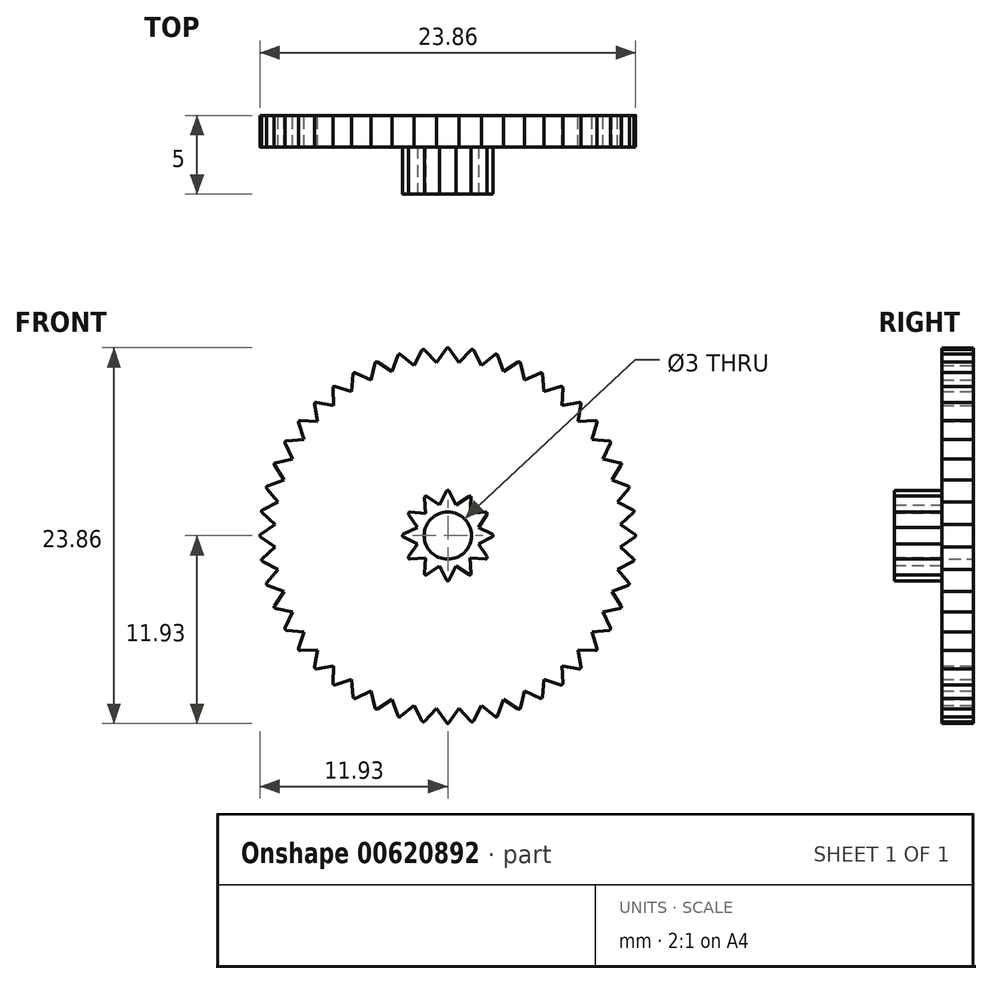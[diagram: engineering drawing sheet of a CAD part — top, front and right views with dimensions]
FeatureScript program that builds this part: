
annotation { "Feature Type Name" : "Feature", "Feature Type Description" : "" }
export const myFeature = defineFeature(function(context is Context, id is Id, definition is map)
    precondition{}
    {
        {
            var Q0;
            Q0=qCreatedBy(makeId("Front.planeOp"),FACE);
            var sketch = newSketch(context, id + "F0", { "sketchPlane" : qUnion([Q0])});
            skCircle(sketch, "E0", {"center": v(0, 0) * mm, "radius": 11 * mm});
            skLineSegment(sketch, "E1", {"start": v(0, 12) * mm, "end": v(0, 11) * mm, "construction": true});
            skCircle(sketch, "E2", {"center": v(0, 0) * mm, "radius": 1.5 * mm});
            skLineSegment(sketch, "E3", {"start": v(0, 12) * mm, "end": v(-0.72, 10.98) * mm});
            skLineSegment(sketch, "E4.MirrorCS", {"start": v(0, 12) * mm, "end": v(0.72, 10.98) * mm});
            skSolve(sketch);
        }
        {
            var Q0;
            Q0=makeQuery(id+"F0.imprint","IMPRINT",FACE,{"disambiguationData":[TD([[makeQuery(id+"F0.imprint","IMPRINT",EDGE,{"derivedFrom":sQuery(id+"F0.wireOp",EDGE,"E2")}),-1.0]])]});
            extrude(context, id + "F1", {"entities" : qUnion([Q0]), "depth" : 2 * mm, "offsetDistance" : 25 * mm});
        }
        {
            var Q0;
            {var subQ0=sQuery(id+"F0.wireOp",EDGE,"E3");Q0=makeQuery(id+"F0.imprint","IMPRINT",FACE,{"disambiguationData":[TD([[makeQuery(id+"F0.imprint","IMPRINT",EDGE,{"derivedFrom":subQ0}),1.0]])]});}
            extrude(context, id + "F2", {"entities" : qUnion([Q0]), "depth" : 2 * mm, "offsetDistance" : 25 * mm});
        }
        {
            var Q0;
            Q0=makeQuery(id+"F2.opExtrude","SWEPT_EDGE",EDGE,{"disambiguationData":[OSD([sQuery(id+"F0.wireOp",EDGE,"E3"),sQuery(id+"F0.wireOp",EDGE,"E4.MirrorCS")])]});
            fillet(context, id + "F3", {"entities" : qUnion([Q0]), "radius" : 0.1 * mm, "tangentPropagation" : true, "allowEdgeOverflow" : false});
        }
        {
            var Q0;
            Q0=makeQuery(id+"F2.opExtrude","SWEPT_BODY",BODY,{"disambiguationData":[OSD([sQuery(id+"F0.wireOp",EDGE,"E0"),sQuery(id+"F0.wireOp",EDGE,"E3"),sQuery(id+"F0.wireOp",EDGE,"E4.MirrorCS")])]});
            var Q1;
            Q1=makeQuery(id+"F1.opExtrude","CAP_EDGE",EDGE,{"disambiguationData":[OSD([sQuery(id+"F0.wireOp",EDGE,"E2")])],"isStart":false});
            circularPattern(context, id + "F4", {"operationType" : NewBodyOperationType.ADD, "entities" : qUnion([Q0]), "axis" : qUnion([Q1]), "angle" : 360 * degree, "instanceCount" : 48, "equalSpace" : true});
        }
        {
            var Q0;
            {var subQ0=sQuery(id+"F0.wireOp",EDGE,"E0");var subQ1=makeQuery(id+"F2.opExtrude","CAP_FACE",FACE,{"disambiguationData":[OSD([subQ0,sQuery(id+"F0.wireOp",EDGE,"E3"),sQuery(id+"F0.wireOp",EDGE,"E4.MirrorCS")])],"isStart":false});Q0=makeQuery(id+"F4.boolean.opBoolean","MERGE",FACE,{"derivedFrom":[makeQuery(id+"F1.opExtrude","CAP_FACE",FACE,{"disambiguationData":[OSD([subQ0,sQuery(id+"F0.wireOp",EDGE,"E2")])],"isStart":false}),subQ1,makeQuery(id+"F4.opPattern","COPY",FACE,{"derivedFrom":subQ1,"instanceName":"1"}),makeQuery(id+"F4.opPattern","COPY",FACE,{"derivedFrom":subQ1,"instanceName":"2"}),makeQuery(id+"F4.opPattern","COPY",FACE,{"derivedFrom":subQ1,"instanceName":"3"}),makeQuery(id+"F4.opPattern","COPY",FACE,{"derivedFrom":subQ1,"instanceName":"4"}),makeQuery(id+"F4.opPattern","COPY",FACE,{"derivedFrom":subQ1,"instanceName":"5"}),makeQuery(id+"F4.opPattern","COPY",FACE,{"derivedFrom":subQ1,"instanceName":"6"}),makeQuery(id+"F4.opPattern","COPY",FACE,{"derivedFrom":subQ1,"instanceName":"7"}),makeQuery(id+"F4.opPattern","COPY",FACE,{"derivedFrom":subQ1,"instanceName":"8"}),makeQuery(id+"F4.opPattern","COPY",FACE,{"derivedFrom":subQ1,"instanceName":"9"}),makeQuery(id+"F4.opPattern","COPY",FACE,{"derivedFrom":subQ1,"instanceName":"10"}),makeQuery(id+"F4.opPattern","COPY",FACE,{"derivedFrom":subQ1,"instanceName":"11"}),makeQuery(id+"F4.opPattern","COPY",FACE,{"derivedFrom":subQ1,"instanceName":"12"}),makeQuery(id+"F4.opPattern","COPY",FACE,{"derivedFrom":subQ1,"instanceName":"13"}),makeQuery(id+"F4.opPattern","COPY",FACE,{"derivedFrom":subQ1,"instanceName":"14"}),makeQuery(id+"F4.opPattern","COPY",FACE,{"derivedFrom":subQ1,"instanceName":"15"}),makeQuery(id+"F4.opPattern","COPY",FACE,{"derivedFrom":subQ1,"instanceName":"16"}),makeQuery(id+"F4.opPattern","COPY",FACE,{"derivedFrom":subQ1,"instanceName":"17"}),makeQuery(id+"F4.opPattern","COPY",FACE,{"derivedFrom":subQ1,"instanceName":"18"}),makeQuery(id+"F4.opPattern","COPY",FACE,{"derivedFrom":subQ1,"instanceName":"19"}),makeQuery(id+"F4.opPattern","COPY",FACE,{"derivedFrom":subQ1,"instanceName":"20"}),makeQuery(id+"F4.opPattern","COPY",FACE,{"derivedFrom":subQ1,"instanceName":"21"}),makeQuery(id+"F4.opPattern","COPY",FACE,{"derivedFrom":subQ1,"instanceName":"22"}),makeQuery(id+"F4.opPattern","COPY",FACE,{"derivedFrom":subQ1,"instanceName":"23"}),makeQuery(id+"F4.opPattern","COPY",FACE,{"derivedFrom":subQ1,"instanceName":"24"}),makeQuery(id+"F4.opPattern","COPY",FACE,{"derivedFrom":subQ1,"instanceName":"25"}),makeQuery(id+"F4.opPattern","COPY",FACE,{"derivedFrom":subQ1,"instanceName":"26"}),makeQuery(id+"F4.opPattern","COPY",FACE,{"derivedFrom":subQ1,"instanceName":"27"}),makeQuery(id+"F4.opPattern","COPY",FACE,{"derivedFrom":subQ1,"instanceName":"28"}),makeQuery(id+"F4.opPattern","COPY",FACE,{"derivedFrom":subQ1,"instanceName":"29"}),makeQuery(id+"F4.opPattern","COPY",FACE,{"derivedFrom":subQ1,"instanceName":"30"}),makeQuery(id+"F4.opPattern","COPY",FACE,{"derivedFrom":subQ1,"instanceName":"31"}),makeQuery(id+"F4.opPattern","COPY",FACE,{"derivedFrom":subQ1,"instanceName":"32"}),makeQuery(id+"F4.opPattern","COPY",FACE,{"derivedFrom":subQ1,"instanceName":"33"}),makeQuery(id+"F4.opPattern","COPY",FACE,{"derivedFrom":subQ1,"instanceName":"34"}),makeQuery(id+"F4.opPattern","COPY",FACE,{"derivedFrom":subQ1,"instanceName":"35"}),makeQuery(id+"F4.opPattern","COPY",FACE,{"derivedFrom":subQ1,"instanceName":"36"}),makeQuery(id+"F4.opPattern","COPY",FACE,{"derivedFrom":subQ1,"instanceName":"37"}),makeQuery(id+"F4.opPattern","COPY",FACE,{"derivedFrom":subQ1,"instanceName":"38"}),makeQuery(id+"F4.opPattern","COPY",FACE,{"derivedFrom":subQ1,"instanceName":"39"}),makeQuery(id+"F4.opPattern","COPY",FACE,{"derivedFrom":subQ1,"instanceName":"40"}),makeQuery(id+"F4.opPattern","COPY",FACE,{"derivedFrom":subQ1,"instanceName":"41"}),makeQuery(id+"F4.opPattern","COPY",FACE,{"derivedFrom":subQ1,"instanceName":"42"}),makeQuery(id+"F4.opPattern","COPY",FACE,{"derivedFrom":subQ1,"instanceName":"43"}),makeQuery(id+"F4.opPattern","COPY",FACE,{"derivedFrom":subQ1,"instanceName":"44"}),makeQuery(id+"F4.opPattern","COPY",FACE,{"derivedFrom":subQ1,"instanceName":"45"}),makeQuery(id+"F4.opPattern","COPY",FACE,{"derivedFrom":subQ1,"instanceName":"46"}),makeQuery(id+"F4.opPattern","COPY",FACE,{"derivedFrom":subQ1,"instanceName":"47"})]});}
            var sketch = newSketch(context, id + "F5", { "sketchPlane" : qUnion([Q0])});
            skCircle(sketch, "E5", {"center": v(0, 0) * mm, "radius": 2 * mm});
            skLineSegment(sketch, "E6", {"start": v(0, 3) * mm, "end": v(0, 2) * mm, "construction": true});
            skLineSegment(sketch, "E7", {"start": v(0, 3) * mm, "end": v(-0.52, 1.93) * mm});
            skLineSegment(sketch, "E8.MirrorCS", {"start": v(0, 3) * mm, "end": v(0.52, 1.93) * mm});
            skSolve(sketch);
        }
        {
            var Q0;
            Q0=makeQuery(id+"F5.imprint","IMPRINT",FACE,{"disambiguationData":[TD([[makeQuery(id+"F5.imprint","IMPRINT",EDGE,{"derivedFrom":makeQuery(id+"F1.opExtrude","CAP_EDGE",EDGE,{"disambiguationData":[OSD([sQuery(id+"F0.wireOp",EDGE,"E2")])],"isStart":false})}),-1.0]])]});
            extrude(context, id + "F6", {"entities" : qUnion([Q0]), "operationType" : NewBodyOperationType.ADD, "depth" : 3 * mm, "offsetDistance" : 25 * mm});
        }
        {
            var Q0;
            {var subQ0=sQuery(id+"F5.wireOp",EDGE,"E7");Q0=makeQuery(id+"F5.imprint","IMPRINT",FACE,{"disambiguationData":[TD([[makeQuery(id+"F5.imprint","IMPRINT",EDGE,{"derivedFrom":subQ0}),1.0]])]});}
            extrude(context, id + "F7", {"entities" : qUnion([Q0]), "depth" : 3 * mm, "offsetDistance" : 25 * mm});
        }
        {
            var Q0;
            Q0=makeQuery(id+"F7.opExtrude","SWEPT_EDGE",EDGE,{"disambiguationData":[OSD([sQuery(id+"F5.wireOp",EDGE,"E7"),sQuery(id+"F5.wireOp",EDGE,"E8.MirrorCS")])]});
            fillet(context, id + "F8", {"entities" : qUnion([Q0]), "radius" : 0.1 * mm, "tangentPropagation" : true, "allowEdgeOverflow" : false});
        }
        {
            var Q0;
            Q0=makeQuery(id+"F7.opExtrude","SWEPT_BODY",BODY,{"disambiguationData":[OSD([sQuery(id+"F5.wireOp",EDGE,"E5"),sQuery(id+"F5.wireOp",EDGE,"E7"),sQuery(id+"F5.wireOp",EDGE,"E8.MirrorCS")])]});
            var Q1;
            Q1=makeQuery(id+"F6.opExtrude","CAP_EDGE",EDGE,{"disambiguationData":[OSD([sQuery(id+"F0.wireOp",EDGE,"E2")])],"isStart":false});
            circularPattern(context, id + "F9", {"operationType" : NewBodyOperationType.ADD, "entities" : qUnion([Q0]), "axis" : qUnion([Q1]), "angle" : 360 * degree, "instanceCount" : 12, "equalSpace" : true});
        }
    });
